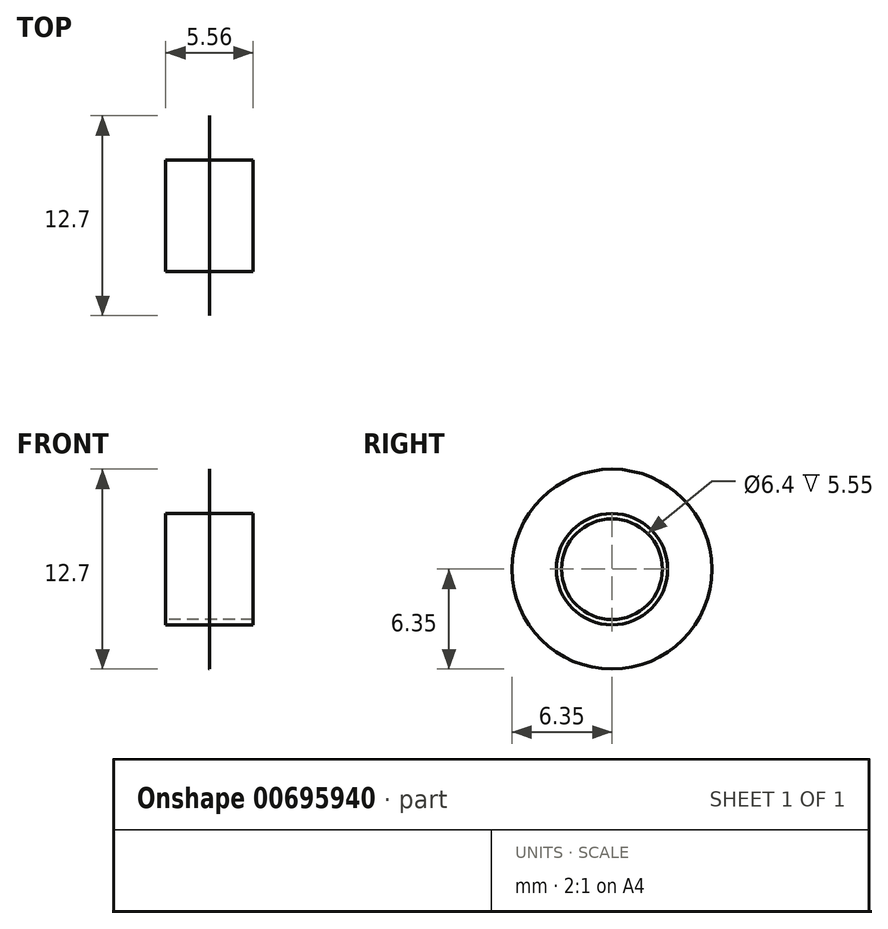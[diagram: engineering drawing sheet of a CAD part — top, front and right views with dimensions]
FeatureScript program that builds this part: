
annotation { "Feature Type Name" : "Feature", "Feature Type Description" : "" }
export const myFeature = defineFeature(function(context is Context, id is Id, definition is map)
    precondition{}
    {
        {
            var Q0;
            Q0=qCreatedBy(makeId("Right.planeOp"),FACE);
            var sketch = newSketch(context, id + "F0", { "sketchPlane" : qUnion([Q0])});
            skCircle(sketch, "E0", {"center": v(0, 0) * mm, "radius": 6.35 * mm});
            skCircle(sketch, "E1", {"center": v(0, 0) * mm, "radius": 3.2 * mm});
            skSolve(sketch);
        }
        {
            var Q0;
            Q0 = qSketchRegion(id + "F0", true);
            extrude(context, id + "F1", {"entities" : qUnion([Q0]), "endBound" : BoundingType.SYMMETRIC, "depth" : 3 / 406.4 * mm, "offsetDistance" : 25 * mm});
        }
        {
            var Q0;
            Q0=qCreatedBy(makeId("Right.planeOp"),FACE);
            var sketch = newSketch(context, id + "F2", { "sketchPlane" : qUnion([Q0])});
            skCircle(sketch, "E2", {"center": v(0, 0) * mm, "radius": 3.54 * mm});
            skCircle(sketch, "E3", {"center": v(0, 0) * mm, "radius": 3.2 * mm});
            skSolve(sketch);
        }
        {
            var Q0;
            Q0 = qSketchRegion(id + "F2", true);
            extrude(context, id + "F3", {"entities" : qUnion([Q0]), "operationType" : NewBodyOperationType.ADD, "endBound" : BoundingType.SYMMETRIC, "depth" : 5.55 * mm, "offsetDistance" : 25 * mm});
        }
    });
